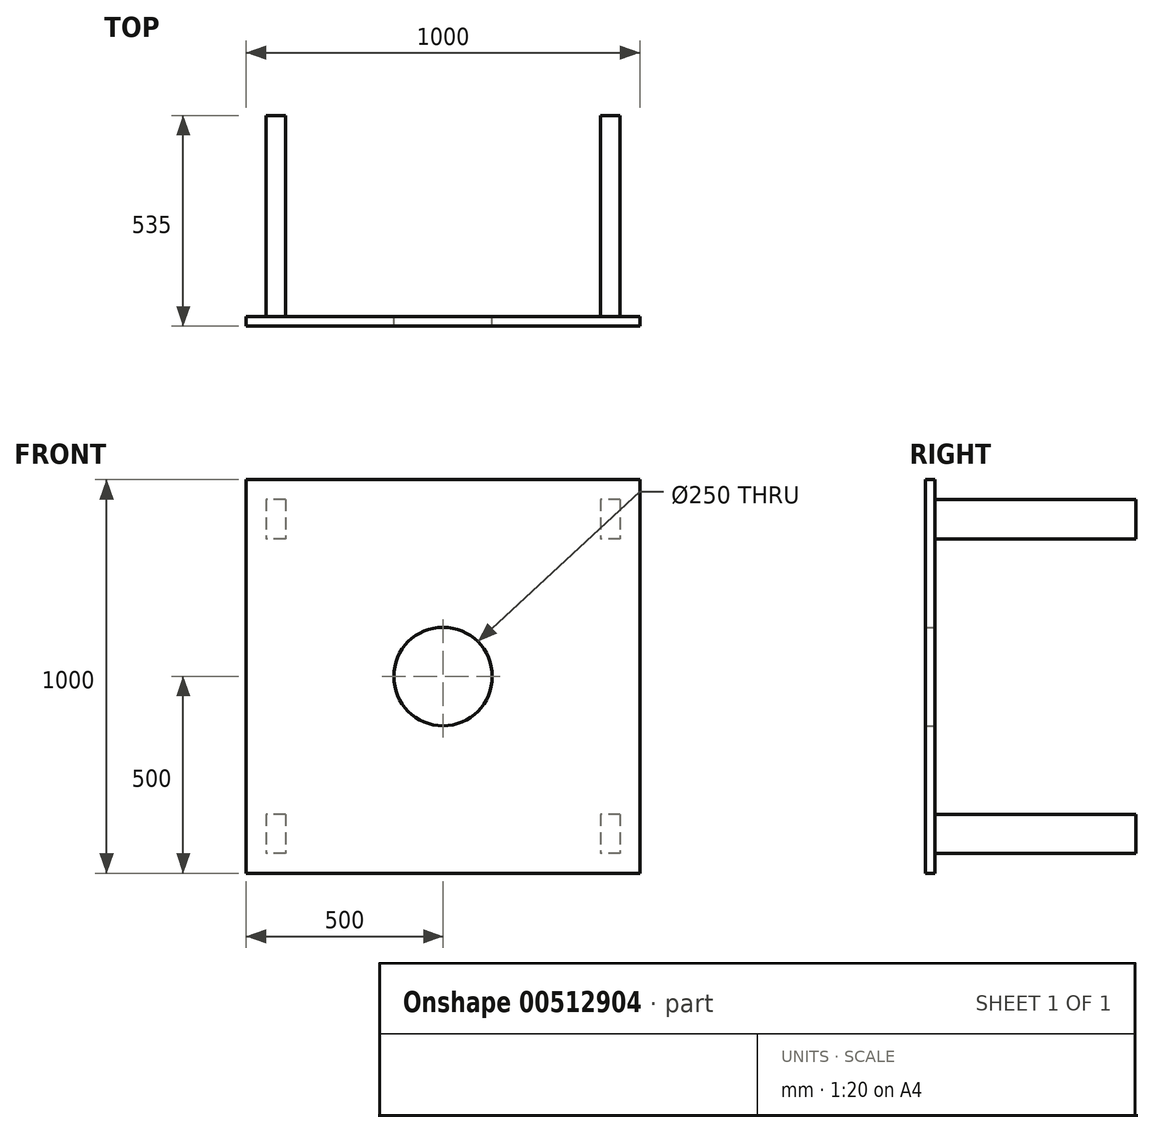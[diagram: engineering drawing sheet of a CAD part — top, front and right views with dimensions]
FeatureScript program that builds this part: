
annotation { "Feature Type Name" : "Feature", "Feature Type Description" : "" }
export const myFeature = defineFeature(function(context is Context, id is Id, definition is map)
    precondition{}
    {
        {
            var Q0;
            Q0=qCreatedBy(makeId("Front.planeOp"),FACE);
            var sketch = newSketch(context, id + "F0", { "sketchPlane" : qUnion([Q0])});
            skLineSegment(sketch, "E0.bottom", {"start": v(0, 0) * mm, "end": v(1000, 0) * mm});
            skLineSegment(sketch, "E0.top", {"start": v(0, -1000) * mm, "end": v(1000, -1000) * mm});
            skLineSegment(sketch, "E0.left", {"start": v(0, 0) * mm, "end": v(0, -1000) * mm});
            skLineSegment(sketch, "E0.right", {"start": v(1000, 0) * mm, "end": v(1000, -1000) * mm});
            skCircle(sketch, "E1", {"center": v(500, -500) * mm, "radius": 125 * mm});
            skSolve(sketch);
        }
        {
            var Q0;
            Q0 = qSketchRegion(id + "F0", true);
            extrude(context, id + "F1", {"entities" : qUnion([Q0]), "depth" : 25 * mm});
        }
        {
            var Q0;
            Q0=makeQuery(id+"F1.opExtrude","CAP_FACE",FACE,{"disambiguationData":[OSD([sQuery(id+"F0.wireOp",EDGE,"E0.bottom"),sQuery(id+"F0.wireOp",EDGE,"E0.top"),sQuery(id+"F0.wireOp",EDGE,"E0.left"),sQuery(id+"F0.wireOp",EDGE,"E0.right"),sQuery(id+"F0.wireOp",EDGE,"E1")])],"isStart":true});
            var sketch = newSketch(context, id + "F2", { "sketchPlane" : qUnion([Q0])});
            skLineSegment(sketch, "E2.bottom", {"start": v(-950, -50) * mm, "end": v(-900, -50) * mm});
            skLineSegment(sketch, "E2.top", {"start": v(-950, -150) * mm, "end": v(-900, -150) * mm});
            skLineSegment(sketch, "E2.left", {"start": v(-950, -50) * mm, "end": v(-950, -150) * mm});
            skLineSegment(sketch, "E2.right", {"start": v(-900, -50) * mm, "end": v(-900, -150) * mm});
            skLineSegment(sketch, "E3.0.1.0", {"start": v(-900, -850) * mm, "end": v(-900, -950) * mm});
            skLineSegment(sketch, "E3.0.1.1", {"start": v(-950, -850) * mm, "end": v(-900, -850) * mm});
            skLineSegment(sketch, "E3.0.1.2", {"start": v(-950, -850) * mm, "end": v(-950, -950) * mm});
            skLineSegment(sketch, "E3.0.1.3", {"start": v(-950, -950) * mm, "end": v(-900, -950) * mm});
            skLineSegment(sketch, "E3.1.0.0", {"start": v(-50, -50) * mm, "end": v(-50, -150) * mm});
            skLineSegment(sketch, "E3.1.0.1", {"start": v(-100, -50) * mm, "end": v(-50, -50) * mm});
            skLineSegment(sketch, "E3.1.0.2", {"start": v(-100, -50) * mm, "end": v(-100, -150) * mm});
            skLineSegment(sketch, "E3.1.0.3", {"start": v(-100, -150) * mm, "end": v(-50, -150) * mm});
            skLineSegment(sketch, "E3.1.1.0", {"start": v(-50, -850) * mm, "end": v(-50, -950) * mm});
            skLineSegment(sketch, "E3.1.1.1", {"start": v(-100, -850) * mm, "end": v(-50, -850) * mm});
            skLineSegment(sketch, "E3.1.1.2", {"start": v(-100, -850) * mm, "end": v(-100, -950) * mm});
            skLineSegment(sketch, "E3.1.1.3", {"start": v(-100, -950) * mm, "end": v(-50, -950) * mm});
            skLineSegment(sketch, "E3.direction1", {"start": v(-950, -150) * mm, "end": v(-100, -150) * mm, "construction": true});
            skLineSegment(sketch, "E3.direction2", {"start": v(-950, -150) * mm, "end": v(-950, -950) * mm, "construction": true});
            skSolve(sketch);
        }
        {
            var Q0;
            Q0 = qSketchRegion(id + "F2", true);
            extrude(context, id + "F3", {"entities" : qUnion([Q0]), "operationType" : NewBodyOperationType.ADD, "depth" : 510 * mm});
        }
    });
